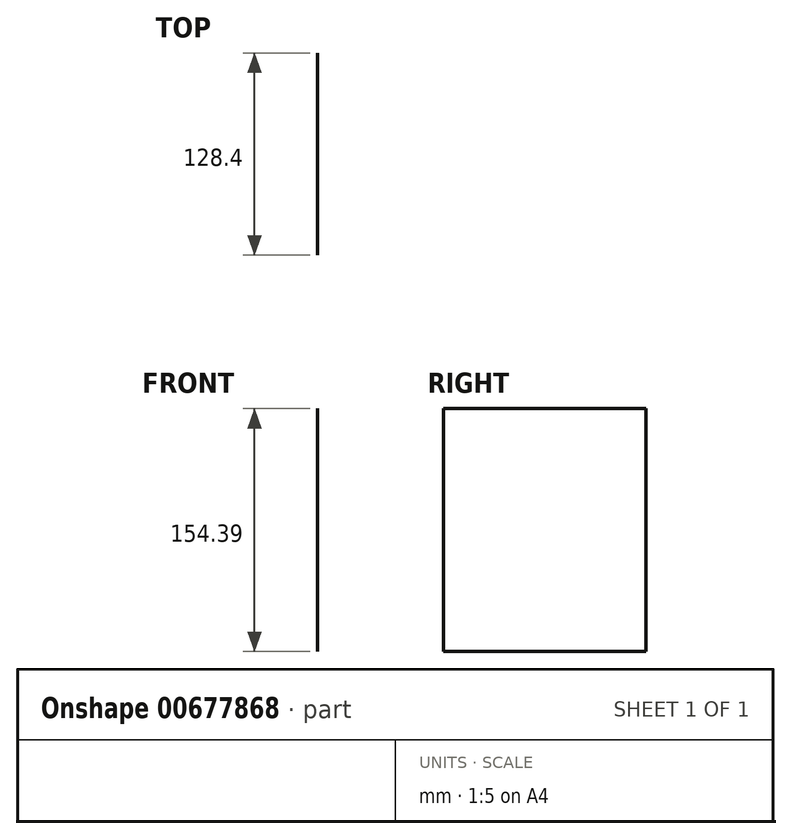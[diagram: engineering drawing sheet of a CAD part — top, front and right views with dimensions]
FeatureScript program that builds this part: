
annotation { "Feature Type Name" : "Feature", "Feature Type Description" : "" }
export const myFeature = defineFeature(function(context is Context, id is Id, definition is map)
    precondition{}
    {
        {
            var Q0;
            Q0=qCreatedBy(makeId("Front.planeOp"),FACE);
            var sketch = newSketch(context, id + "F0", { "sketchPlane" : qUnion([Q0])});
            skLineSegment(sketch, "E0.bottom", {"start": v(70.4, -58.47) * mm, "end": v(37.54, -58.47) * mm});
            skLineSegment(sketch, "E0.top", {"start": v(70.4, 95.92) * mm, "end": v(37.54, 95.92) * mm});
            skLineSegment(sketch, "E0.left", {"start": v(70.4, -58.47) * mm, "end": v(70.4, 95.92) * mm});
            skLineSegment(sketch, "E0.right", {"start": v(37.54, -58.47) * mm, "end": v(37.54, 95.92) * mm});
            skPoint(sketch, "E0.middle", {"position": v(53.97, 18.72) * mm});
            skSolve(sketch);
        }
        {
            var Q0;
            Q0=sQuery(id+"F0.wireOp",EDGE,"E0.left");
            extrude(context, id + "F1", {"bodyType" : ToolBodyType.SURFACE, "surfaceEntities" : qUnion([Q0]), "oppositeDirection" : true, "depth" : 56.8 * mm, "offsetDistance" : 25 * mm, "hasSecondDirection" : true, "secondDirectionOppositeDirection" : false, "secondDirectionDepth" : 71.6 * mm});
        }
    });
